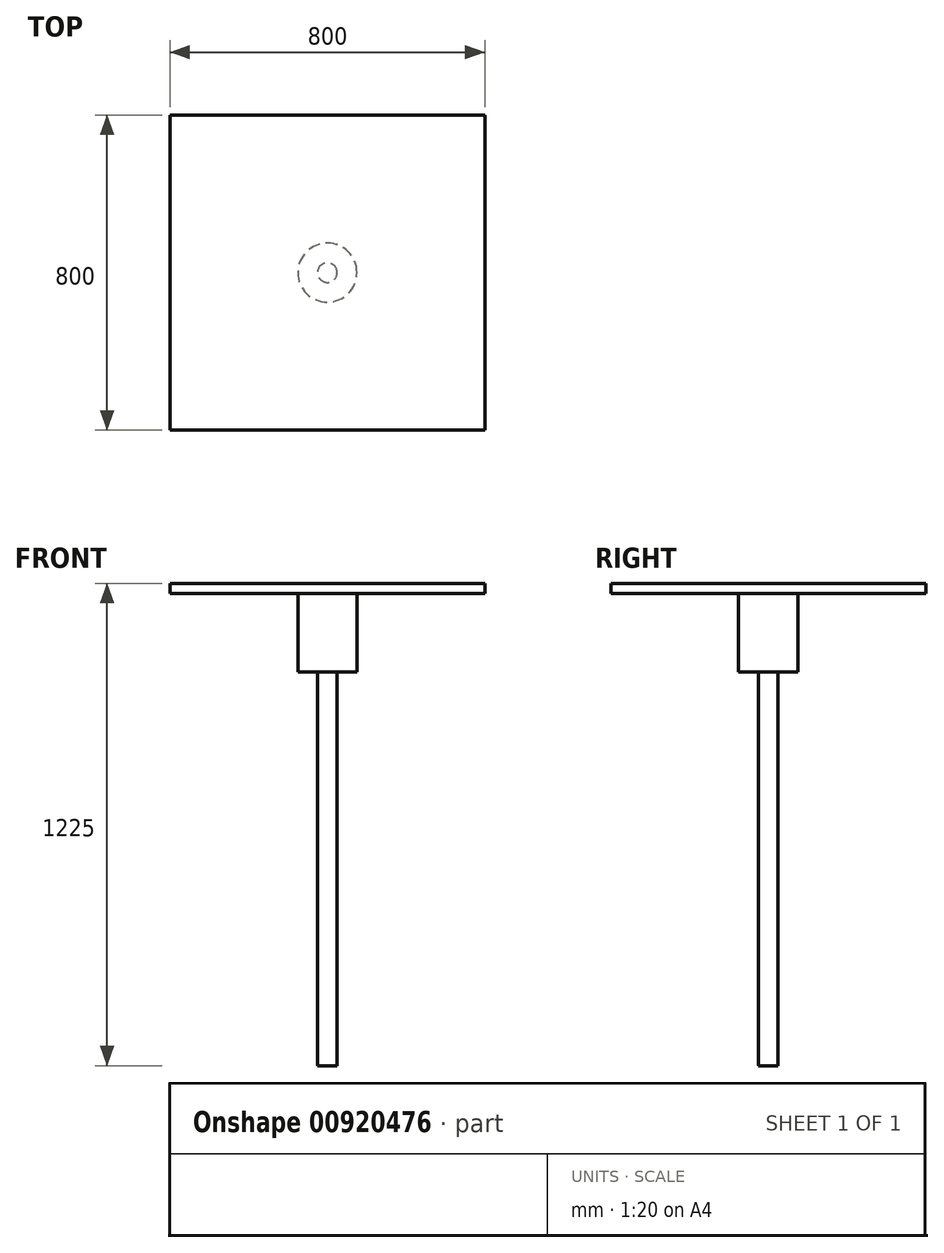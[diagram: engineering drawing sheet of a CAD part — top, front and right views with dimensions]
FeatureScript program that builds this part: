
annotation { "Feature Type Name" : "Feature", "Feature Type Description" : "" }
export const myFeature = defineFeature(function(context is Context, id is Id, definition is map)
    precondition{}
    {
        {
            var Q0;
            Q0=qCreatedBy(makeId("Top.planeOp"),FACE);
            var sketch = newSketch(context, id + "F0", { "sketchPlane" : qUnion([Q0])});
            skCircle(sketch, "E0", {"center": v(0, 0) * mm, "radius": 25 * mm});
            skSolve(sketch);
        }
        {
            var Q0;
            Q0=makeQuery(id+"F0.imprint","IMPRINT",FACE,{"disambiguationData":[TD([[makeQuery(id+"F0.imprint","IMPRINT",EDGE,{"derivedFrom":sQuery(id+"F0.wireOp",EDGE,"E0")}),1.0]])]});
            extrude(context, id + "F1", {"entities" : qUnion([Q0]), "depth" : 1000 * mm, "offsetDistance" : 25 * mm});
        }
        {
            var Q0;
            Q0=makeQuery(id+"F1.opExtrude","CAP_FACE",FACE,{"disambiguationData":[OSD([sQuery(id+"F0.wireOp",EDGE,"E0")])],"isStart":false});
            var sketch = newSketch(context, id + "F2", { "sketchPlane" : qUnion([Q0])});
            skCircle(sketch, "E1", {"center": v(0, 0) * mm, "radius": 75 * mm});
            skSolve(sketch);
        }
        {
            var Q0;
            Q0=makeQuery(id+"F2.imprint","IMPRINT",FACE,{"disambiguationData":[TD([[makeQuery(id+"F2.imprint","IMPRINT",EDGE,{"derivedFrom":makeQuery(id+"F1.opExtrude","CAP_EDGE",EDGE,{"disambiguationData":[OSD([sQuery(id+"F0.wireOp",EDGE,"E0")])],"isStart":false})}),1.0]])]});
            var Q1;
            Q1=makeQuery(id+"F2.imprint","IMPRINT",FACE,{"disambiguationData":[TD([[makeQuery(id+"F2.imprint","IMPRINT",EDGE,{"derivedFrom":sQuery(id+"F2.wireOp",EDGE,"E1")}),1.0]])]});
            extrude(context, id + "F3", {"entities" : qUnion([Q0, Q1]), "operationType" : NewBodyOperationType.ADD, "depth" : 200 * mm, "offsetDistance" : 25 * mm});
        }
        {
            var Q0;
            Q0=makeQuery(id+"F3.opExtrude","CAP_FACE",FACE,{"disambiguationData":[OSD([sQuery(id+"F2.wireOp",EDGE,"E1")])],"isStart":false});
            var sketch = newSketch(context, id + "F4", { "sketchPlane" : qUnion([Q0])});
            skLineSegment(sketch, "E2.bottom", {"start": v(-400, -400) * mm, "end": v(400, -400) * mm});
            skLineSegment(sketch, "E2.top", {"start": v(-400, 400) * mm, "end": v(400, 400) * mm});
            skLineSegment(sketch, "E2.left", {"start": v(-400, -400) * mm, "end": v(-400, 400) * mm});
            skLineSegment(sketch, "E2.right", {"start": v(400, -400) * mm, "end": v(400, 400) * mm});
            skPoint(sketch, "E2.middle", {"position": v(0, 0) * mm});
            skSolve(sketch);
        }
        {
            var Q0;
            Q0 = qSketchRegion(id + "F4", true);
            extrude(context, id + "F5", {"entities" : qUnion([Q0]), "operationType" : NewBodyOperationType.ADD, "depth" : 25 * mm, "offsetDistance" : 25 * mm});
        }
    });
